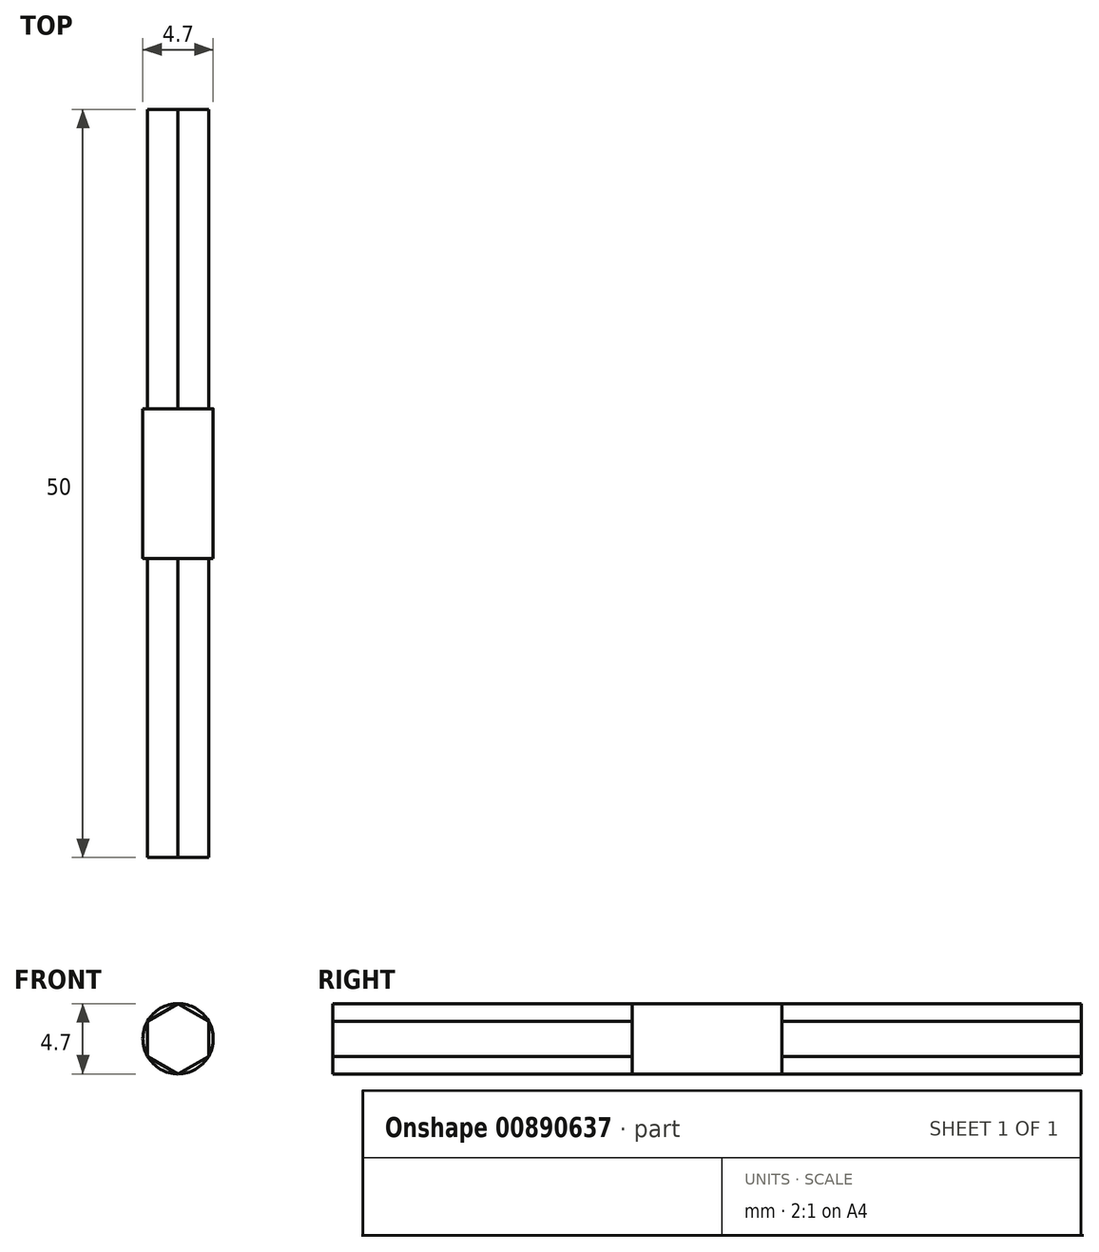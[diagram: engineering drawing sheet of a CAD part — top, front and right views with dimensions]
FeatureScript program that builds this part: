
annotation { "Feature Type Name" : "Feature", "Feature Type Description" : "" }
export const myFeature = defineFeature(function(context is Context, id is Id, definition is map)
    precondition{}
    {
        {
            var Q0;
            Q0=qCreatedBy(makeId("Front.planeOp"),FACE);
            var sketch = newSketch(context, id + "F0", { "sketchPlane" : qUnion([Q0])});
            skCircle(sketch, "E0", {"center": v(0, 0) * mm, "radius": 2.35 * mm});
            skCircle(sketch, "E1.cCircle", {"center": v(0, 0) * mm, "radius": 2.35 * mm, "construction": true});
            skLineSegment(sketch, "E1.0", {"start": v(0, 2.35) * mm, "end": v(2.04, 1.18) * mm});
            skLineSegment(sketch, "E1.1", {"start": v(2.04, 1.18) * mm, "end": v(2.04, -1.17) * mm});
            skLineSegment(sketch, "E1.2", {"start": v(2.04, -1.17) * mm, "end": v(0, -2.35) * mm});
            skLineSegment(sketch, "E1.3", {"start": v(0, -2.35) * mm, "end": v(-2.04, -1.18) * mm});
            skLineSegment(sketch, "E1.4", {"start": v(-2.04, -1.18) * mm, "end": v(-2.04, 1.17) * mm});
            skLineSegment(sketch, "E1.5", {"start": v(-2.04, 1.17) * mm, "end": v(0, 2.35) * mm});
            skSolve(sketch);
        }
        {
            var Q0;
            Q0=makeQuery(id+"F0.imprint","IMPRINT",FACE,{"disambiguationData":[TD([[makeQuery(id+"F0.imprint","IMPRINT",EDGE,{"derivedFrom":sQuery(id+"F0.wireOp",EDGE,"E1.0")}),-1.0]])]});
            extrude(context, id + "F1", {"entities" : qUnion([Q0]), "depth" : 20 * mm, "offsetDistance" : 25 * mm, "hasSecondDirection" : true, "secondDirectionOppositeDirection" : true, "secondDirectionDepth" : 30 * mm});
        }
        {
            var Q0;
            {var subQ0=sQuery(id+"F0.wireOp",EDGE,"E1.5");Q0=makeQuery(id+"F0.imprint","IMPRINT",FACE,{"disambiguationData":[TD([[makeQuery(id+"F0.imprint","IMPRINT",EDGE,{"derivedFrom":subQ0}),1.0]])]});}
            var Q1;
            {var subQ0=sQuery(id+"F0.wireOp",EDGE,"E1.0");Q1=makeQuery(id+"F0.imprint","IMPRINT",FACE,{"disambiguationData":[TD([[makeQuery(id+"F0.imprint","IMPRINT",EDGE,{"derivedFrom":subQ0}),1.0]])]});}
            var Q2;
            {var subQ0=sQuery(id+"F0.wireOp",EDGE,"E1.1");Q2=makeQuery(id+"F0.imprint","IMPRINT",FACE,{"disambiguationData":[TD([[makeQuery(id+"F0.imprint","IMPRINT",EDGE,{"derivedFrom":subQ0}),1.0]])]});}
            var Q3;
            {var subQ0=sQuery(id+"F0.wireOp",EDGE,"E1.2");Q3=makeQuery(id+"F0.imprint","IMPRINT",FACE,{"disambiguationData":[TD([[makeQuery(id+"F0.imprint","IMPRINT",EDGE,{"derivedFrom":subQ0}),1.0]])]});}
            var Q4;
            Q4=makeQuery(id+"F0.imprint","IMPRINT",FACE,{"disambiguationData":[TD([[makeQuery(id+"F0.imprint","IMPRINT",EDGE,{"derivedFrom":sQuery(id+"F0.wireOp",EDGE,"E1.0")}),-1.0]])]});
            var Q5;
            {var subQ0=sQuery(id+"F0.wireOp",EDGE,"E1.4");Q5=makeQuery(id+"F0.imprint","IMPRINT",FACE,{"disambiguationData":[TD([[makeQuery(id+"F0.imprint","IMPRINT",EDGE,{"derivedFrom":subQ0}),1.0]])]});}
            var Q6;
            {var subQ0=sQuery(id+"F0.wireOp",EDGE,"E1.3");Q6=makeQuery(id+"F0.imprint","IMPRINT",FACE,{"disambiguationData":[TD([[makeQuery(id+"F0.imprint","IMPRINT",EDGE,{"derivedFrom":subQ0}),1.0]])]});}
            extrude(context, id + "F2", {"entities" : qUnion([Q0, Q1, Q2, Q3, Q4, Q5, Q6]), "operationType" : NewBodyOperationType.ADD, "oppositeDirection" : true, "depth" : 10 * mm, "offsetDistance" : 25 * mm});
        }
    });
